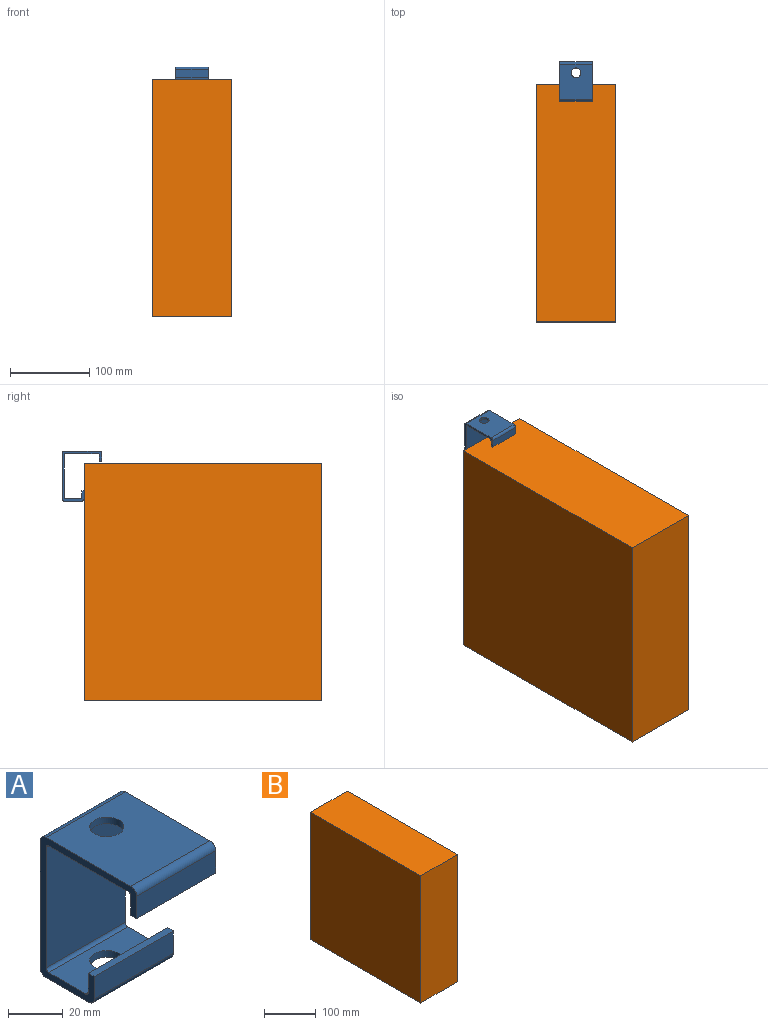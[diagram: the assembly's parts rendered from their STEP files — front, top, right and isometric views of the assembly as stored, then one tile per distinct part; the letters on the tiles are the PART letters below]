
ASSEMBLY  parts=2 mates=1
PART A: 24 faces, bbox 41x50x63 mm
  f0: cylinder r=1.5mm len=41mm, axis (-1,0,0), area 96.6mm2, adj f1,f19,f20,f21
  f1: plane 41x41mm, normal (0,0,-1), area 1558.3mm2, adj f0,f2,f20,f21,f22
  f2: cylinder r=1.5mm len=41mm, axis (-1,0,0), area 96.6mm2, adj f1,f3,f20,f21
  f3: plane 54x41mm, normal (0,-1,0), area 2214mm2, adj f2,f4,f20,f21
  f4: cylinder r=1.5mm len=41mm, axis (-1,0,0), area 96.6mm2, adj f3,f5,f20,f21
  f5: plane 41x19mm, normal (0,0,1), area 656.3mm2, adj f4,f6,f20,f21,f23
  f6: cylinder r=1.5mm len=41mm, axis (-1,0,0), area 96.6mm2, adj f5,f7,f20,f21
  f7: plane 41x8.5mm, normal (0,1,0), area 348.5mm2, adj f6,f8,f20,f21
  f8: plane 41x3mm, normal (0,0,1), area 123mm2, adj f7,f9,f20,f21
  f9: plane 41x10mm, normal (0,-1,0), area 410mm2, adj f8,f10,f20,f21
  f10: cylinder r=3mm len=41mm, axis (-1,0,0), area 193.2mm2, adj f9,f11,f20,f21
  f11: plane 41x22mm, normal (0,0,-1), area 779.3mm2, adj f10,f12,f20,f21,f23
  f12: cylinder r=3mm len=41mm, axis (-1,0,0), area 193.2mm2, adj f11,f13,f20,f21
  f13: plane 57x41mm, normal (0,1,0), area 2337mm2, adj f12,f14,f20,f21
  f14: cylinder r=3mm len=41mm, axis (-1,0,0), area 193.2mm2, adj f13,f15,f20,f21
  f15: plane 44x41mm, normal (0,0,1), area 1681.3mm2, adj f14,f16,f20,f21,f22
  f16: cylinder r=3mm len=41mm, axis (-1,0,0), area 193.2mm2, adj f15,f17,f20,f21
  f17: plane 41x10mm, normal (0,-1,0), area 410mm2, adj f16,f18,f20,f21
  f18: plane 41x3mm, normal (0,0,-1), area 123mm2, adj f17,f19,f20,f21
  f19: plane 41x8.5mm, normal (0,1,0), area 348.5mm2, adj f0,f18,f20,f21
  f20: plane 63x50mm, normal (1,0,0), area 459.2mm2, adj f0,f1,f2,f3,f4,f5,f6,f7
  f21: plane 63x50mm, normal (-1,0,0), area 459.2mm2, adj f0,f1,f2,f3,f4,f5,f6,f7
  f22: cylinder r=6.25mm len=12.5mm, axis (0,0,1), area 117.8mm2, adj f1,f15
  f23: cylinder r=6.25mm len=12.5mm, axis (0,0,1), area 117.8mm2, adj f5,f11
PART B: 6 faces, bbox 100x300x300 mm
  f0: plane 300x100mm, normal (0,0,1), area 30000mm2, adj f1,f3,f4,f5
  f1: plane 300x100mm, normal (0,-1,0), area 30000mm2, adj f0,f2,f4,f5
  f2: plane 300x100mm, normal (0,0,-1), area 30000mm2, adj f1,f3,f4,f5
  f3: plane 300x100mm, normal (0,1,0), area 30000mm2, adj f0,f2,f4,f5
  f4: plane 300x300mm, normal (1,0,0), area 90000mm2, adj f0,f1,f2,f3
  f5: plane 300x300mm, normal (-1,0,0), area 90000mm2, adj f0,f1,f2,f3
PLACE A t=(-28.78,-63.39,25.69)mm
PLACE B t=(-78.78,38.94,22.92)mm fixed
MATE fastened A.f9 <-> B.f3  axis (0,-1,0) through (-28.78,-66.39,42.19)mm
